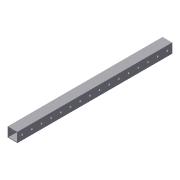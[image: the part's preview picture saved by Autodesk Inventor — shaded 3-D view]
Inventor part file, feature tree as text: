
AUTODESK INVENTOR PART (.ipt)
format: ipt  version: 2012 (Build 160160000, 160)  size: 109,568 bytes
history: native  units: in
note: dims shown in document units (in); Inventor stores cm internally (conversion verified against a paired STEP export)
features: extrude x2, sketch x2, shell x1, pattern_linear x1
ambient origin geometry x8: Origin, YZ Plane, XZ Plane, XY Plane, X Axis, Y Axis, Z Axis, Center Point
bodies: Solid1 (feature_tree)
feature tree (6):
  extrude  "Extrusion1"  Depth=1.0in
  shell  "Shell1"  Thickness=16.0in
  extrude  "Extrusion2"  Depth=0.1875in
  pattern_linear  "Rectangular Pattern1"  Spacing1=0.5in  [1 undecoded]
  sketch  "Sketch1"  dims[d0=1.0in d1=1.0in d2=16.0in d3=0.0in]
  sketch  "Sketch2"  dims[d4=0.0625in d5=0.1875in d6=0.5in d7=0.5in d8=16.0in d9=0.0in d10=6.2992in d12=1.0in]
note: 1 required parameter value undecoded (feature->parameter linkage not recoverable at this tier; creation-order binding heuristic only, values carry confidence <= 0.55)
